# Revit family: Practibox_S_18_modules_encastré_réf_137006_à_137179
name_source: partatom
category: Equipement électrique
revit_build: Autodesk Revit 2018 (Build: 20170223_1515(x64)
units: mm (PartAtom-declared; Revit-internal decimal feet)

## family parameters
Basée sur le plan de construction = Non
Configuration du panneau = Deux colonnes, circuits au sein
Cote de connecteur circulaire = Utiliser le diamètre
Couper avec des vides une fois chargée = Non
Numéro OmniClass = 23.80.30.11.17
Partagée = Non
Point de calcul de pièce = Non
Titre OmniClass = Distribution Boards and Control Panels
Toujours verticalement = Oui
Type d'élément = Tableau de raccordement

## types (32) — shared parameters
Conditions Générale d'Utilisation = https://export.legrand.com
Fabricant = "Legrand"
Largeur = 436 mm  [stored 1.43045 ft]
URL = www.legrand.com

## per-type parameters (varying)
| type | 1R | 2R | 3R | 4R | Bornier N | Bornier T | Hauteur | Ina | porte B 1 r | porte B 2 r | porte B 3 r | porte B 4 r | porte T 1 r | porte T 2 r | porte T 3 r | porte T 4 r | porte blanche | porte transparente | profondeur | taille |
| Practibox_S_36_modules_encastré_137027 | Non | Oui | Non | Non |  |  | 385 mm  [stored 1.26312 ft] | 90 A | Non | Oui | Non | Non | Non | Non | Non | Non | Oui | Non | 103 mm  [stored 0.337927 ft] | 2 rangée |
| Practibox_S_54_modules_encastré_137028 | Non | Non | Oui | Non |  |  | 615 mm  [stored 2.01772 ft] | 90 A | Non | Non | Oui | Non | Non | Non | Non | Non | Oui | Non | 103 mm  [stored 0.337927 ft] | 3 rangée |
| Practibox_S_72_modules_encastré_137029 | Non | Non | Non | Oui |  |  | 765 mm  [stored 2.50984 ft] | 90 A | Non | Non | Non | Oui | Non | Non | Non | Non | Oui | Non | 103 mm  [stored 0.337927 ft] | 4 rangée |
| Practibox_S_18_modules_encastré_137026 | Oui | Non | Non | Non |  |  | 235 mm  [stored 0.770997 ft] | 63 A | Oui | Non | Non | Non | Non | Non | Non | Non | Oui | Non | 102 mm | 1 rangée |
| Practibox_S_18_modules_encastré_137036 | Oui | Non | Non | Non |  |  | 235 mm  [stored 0.770997 ft] | 63 A | Non | Non | Non | Non | Oui | Non | Non | Non | Non | Oui | 102 mm | 1 rangée |
| Practibox_S_18_modules_encastré_137176 | Oui | Non | Non | Non | 17 départs Icc 10kA | 17 départs Icc 10kA | 235 mm  [stored 0.770997 ft] | 63 A | Non | Non | Non | Non | Oui | Non | Non | Non | Non | Oui | 102 mm | 1 rangée |
| Practibox_S_18_modules_encastré_137166 | Oui | Non | Non | Non | 17 départs Icc 10kA | 17 départs Icc 10kA | 235 mm  [stored 0.770997 ft] | 63 A | Oui | Non | Non | Non | Non | Non | Non | Non | Oui | Non | 102 mm | 1 rangée |
| Practibox_S_36_modules_encastré_137037 | Non | Oui | Non | Non |  |  | 385 mm  [stored 1.26312 ft] | 90 A | Non | Non | Non | Non | Non | Oui | Non | Non | Non | Oui | 103 mm  [stored 0.337927 ft] | 2 rangée |
| Practibox_S_36_modules_encastré_137177 | Non | Oui | Non | Non | 27 départs Icc 10kA | 27 départs Icc 10kA | 385 mm  [stored 1.26312 ft] | 90 A | Non | Non | Non | Non | Non | Oui | Non | Non | Non | Oui | 103 mm  [stored 0.337927 ft] | 2 rangée |
| Practibox_S_36_modules_encastré_137167 | Non | Oui | Non | Non | 27 départs Icc 10kA | 27 départs Icc 10kA | 385 mm  [stored 1.26312 ft] | 90 A | Non | Oui | Non | Non | Non | Non | Non | Non | Oui | Non | 103 mm  [stored 0.337927 ft] | 2 rangée |
| Practibox_S_54_modules_encastré_137038 | Non | Non | Oui | Non |  |  | 615 mm  [stored 2.01772 ft] | 90 A | Non | Non | Non | Non | Non | Non | Oui | Non | Non | Oui | 103 mm  [stored 0.337927 ft] | 3 rangée |
| Practibox_S_54_modules_encastré_137168 | Non | Non | Oui | Non | 27 départs Icc 10kA | 27 départs Icc 10kA | 615 mm  [stored 2.01772 ft] | 90 A | Non | Non | Oui | Non | Non | Non | Non | Non | Oui | Non | 103 mm  [stored 0.337927 ft] | 3 rangée |
| Practibox_S_72_modules_encastré_137039 | Non | Non | Non | Oui |  |  | 765 mm  [stored 2.50984 ft] | 90 A | Non | Non | Non | Non | Non | Non | Non | Oui | Non | Oui | 103 mm  [stored 0.337927 ft] | 4 rangée |
| Practibox_S_72_modules_encastré_137169 | Non | Non | Non | Oui | 27 départs Icc 10kA | 27 départs Icc 10kA | 765 mm  [stored 2.50984 ft] | 90 A | Non | Non | Non | Oui | Non | Non | Non | Non | Oui | Non | 103 mm  [stored 0.337927 ft] | 4 rangée |
| Practibox_S_72_modules_encastré_137179 | Non | Non | Non | Oui | 27 départs Icc 10kA | 27 départs Icc 10kA | 765 mm  [stored 2.50984 ft] | 90 A | Non | Non | Non | Non | Non | Non | Non | Oui | Non | Oui | 103 mm  [stored 0.337927 ft] | 4 rangée |
| Practibox_S_18_modules_encastré_137006 | Oui | Non | Non | Non |  |  | 235 mm  [stored 0.770997 ft] | 63 A | Oui | Non | Non | Non | Non | Non | Non | Non | Oui | Non | 102 mm | 1 rangée |
| Practibox_S_18_modules_encastré_137016 | Oui | Non | Non | Non |  |  | 235 mm  [stored 0.770997 ft] | 63 A | Non | Non | Non | Non | Oui | Non | Non | Non | Non | Oui | 102 mm | 1 rangée |
| Practibox_S_18_modules_encastré_137156 | Oui | Non | Non | Non | 17 départs Icc 10kA | 17 départs Icc 10kA | 235 mm  [stored 0.770997 ft] | 63 A | Non | Non | Non | Non | Oui | Non | Non | Non | Non | Oui | 102 mm | 1 rangée |
| Practibox_S_18_modules_encastré_137146 | Oui | Non | Non | Non | 17 départs Icc 10kA | 17 départs Icc 10kA | 235 mm  [stored 0.770997 ft] | 63 A | Oui | Non | Non | Non | Non | Non | Non | Non | Oui | Non | 102 mm | 1 rangée |
| Practibox_S_36_modules_encastré_137007 | Non | Oui | Non | Non |  |  | 385 mm  [stored 1.26312 ft] | 90 A | Non | Oui | Non | Non | Non | Non | Non | Non | Oui | Non | 103 mm  [stored 0.337927 ft] | 2 rangée |
| Practibox_S_36_modules_encastré_137017 | Non | Oui | Non | Non |  |  | 385 mm  [stored 1.26312 ft] | 90 A | Non | Non | Non | Non | Non | Oui | Non | Non | Non | Oui | 103 mm  [stored 0.337927 ft] | 2 rangée |
| Practibox_S_36_modules_encastré_137157 | Non | Oui | Non | Non | 27 départs Icc 10kA | 27 départs Icc 10kA | 385 mm  [stored 1.26312 ft] | 90 A | Non | Non | Non | Non | Non | Oui | Non | Non | Non | Oui | 103 mm  [stored 0.337927 ft] | 2 rangée |
| Practibox_S_36_modules_encastré_137147 | Non | Oui | Non | Non | 27 départs Icc 10kA | 27 départs Icc 10kA | 385 mm  [stored 1.26312 ft] | 90 A | Non | Oui | Non | Non | Non | Non | Non | Non | Oui | Non | 103 mm  [stored 0.337927 ft] | 2 rangée |
| Practibox_S_54_modules_encastré_137008 | Non | Non | Oui | Non |  |  | 615 mm  [stored 2.01772 ft] | 90 A | Non | Non | Oui | Non | Non | Non | Non | Non | Oui | Non | 103 mm  [stored 0.337927 ft] | 3 rangée |
| Practibox_S_54_modules_encastré_137018 | Non | Non | Oui | Non |  |  | 615 mm  [stored 2.01772 ft] | 90 A | Non | Non | Non | Non | Non | Non | Oui | Non | Non | Oui | 103 mm  [stored 0.337927 ft] | 3 rangée |
| Practibox_S_54_modules_encastré_137158 | Non | Non | Oui | Non | 27 départs Icc 10kA | 27 départs Icc 10kA | 615 mm  [stored 2.01772 ft] | 90 A | Non | Non | Non | Non | Non | Non | Oui | Non | Non | Oui | 103 mm  [stored 0.337927 ft] | 3 rangée |
| Practibox_S_54_modules_encastré_137148 | Non | Non | Oui | Non | 27 départs Icc 10kA | 27 départs Icc 10kA | 615 mm  [stored 2.01772 ft] | 90 A | Non | Non | Oui | Non | Non | Non | Non | Non | Oui | Non | 103 mm  [stored 0.337927 ft] | 3 rangée |
| Practibox_S_72_modules_encastré_137009 | Non | Non | Non | Oui |  |  | 765 mm  [stored 2.50984 ft] | 90 A | Non | Non | Non | Oui | Non | Non | Non | Non | Oui | Non | 103 mm  [stored 0.337927 ft] | 4 rangée |
| Practibox_S_72_modules_encastré_137019 | Non | Non | Non | Oui |  |  | 765 mm  [stored 2.50984 ft] | 90 A | Non | Non | Non | Non | Non | Non | Non | Oui | Non | Oui | 103 mm  [stored 0.337927 ft] | 4 rangée |
| Practibox_S_72_modules_encastré_137159 | Non | Non | Non | Oui | 27 départs Icc 10kA | 27 départs Icc 10kA | 765 mm  [stored 2.50984 ft] | 90 A | Non | Non | Non | Non | Non | Non | Non | Oui | Non | Oui | 103 mm  [stored 0.337927 ft] | 4 rangée |
| Practibox_S_72_modules_encastré_137149 | Non | Non | Non | Oui | 27 départs Icc 10kA | 27 départs Icc 10kA | 765 mm  [stored 2.50984 ft] | 90 A | Non | Non | Non | Oui | Non | Non | Non | Non | Oui | Non | 103 mm  [stored 0.337927 ft] | 4 rangée |
| Practibox_S_54_modules_encastré_137178 | Non | Non | Oui | Non | 27 départs Icc 10kA | 27 départs Icc 10kA | 615 mm  [stored 2.01772 ft] | 90 A | Non | Non | Non | Non | Non | Non | Oui | Non | Non | Oui | 103 mm  [stored 0.337927 ft] | 3 rangée |

note: column(s) folded — value = type name in every type: Description

note: [stored X ft] marks values corroborated as IEEE doubles in the binary element streams (Revit-internal decimal feet)
